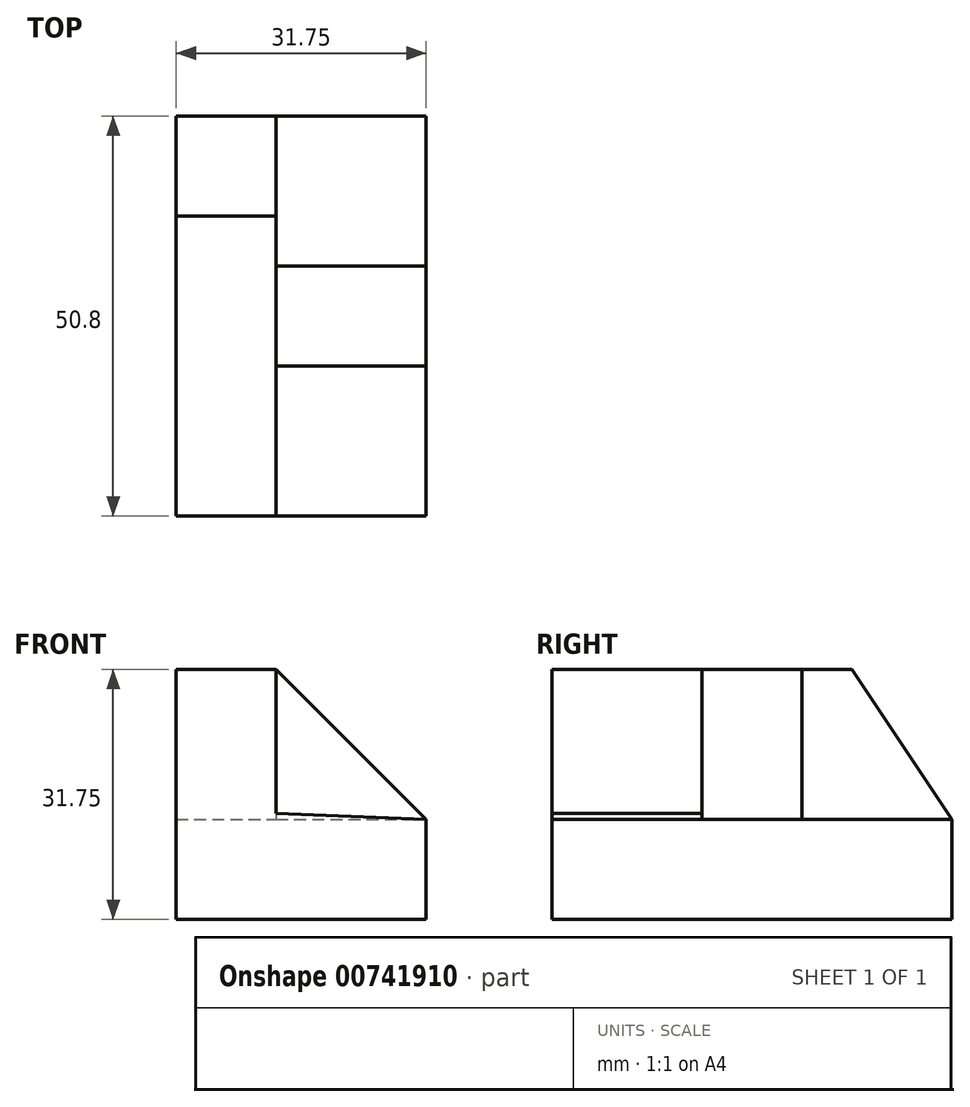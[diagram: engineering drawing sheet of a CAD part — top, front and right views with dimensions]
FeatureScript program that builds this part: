
annotation { "Feature Type Name" : "Feature", "Feature Type Description" : "" }
export const myFeature = defineFeature(function(context is Context, id is Id, definition is map)
    precondition{}
    {
        {
            var Q0;
            Q0=qCreatedBy(makeId("Right.planeOp"),FACE);
            var sketch = newSketch(context, id + "F0", { "sketchPlane" : qUnion([Q0])});
            skLineSegment(sketch, "E0", {"start": v(0, 31.75) * mm, "end": v(0, 0) * mm});
            skLineSegment(sketch, "E1", {"start": v(0, 0) * mm, "end": v(-50.8, 0) * mm});
            skLineSegment(sketch, "E2", {"start": v(-50.8, 0) * mm, "end": v(-50.8, 31.75) * mm});
            skLineSegment(sketch, "E3", {"start": v(-50.8, 31.75) * mm, "end": v(0, 31.75) * mm});
            skSolve(sketch);
        }
        {
            var Q0;
            Q0=makeQuery(id+"F0.imprint","IMPRINT",FACE,{"disambiguationData":[TD([[makeQuery(id+"F0.imprint","IMPRINT",EDGE,{"derivedFrom":sQuery(id+"F0.wireOp",EDGE,"E0")}),-1.0]])]});
            extrude(context, id + "F1", {"entities" : qUnion([Q0]), "depth" : 31.75 * mm, "offsetDistance" : 25.4 * mm});
        }
        {
            var Q0;
            Q0=makeQuery(id+"F1.opExtrude","CAP_FACE",FACE,{"disambiguationData":[OSD([sQuery(id+"F0.wireOp",EDGE,"E0"),sQuery(id+"F0.wireOp",EDGE,"E1"),sQuery(id+"F0.wireOp",EDGE,"E2"),sQuery(id+"F0.wireOp",EDGE,"E3")])],"isStart":false});
            var sketch = newSketch(context, id + "F2", { "sketchPlane" : qUnion([Q0])});
            skLineSegment(sketch, "E4", {"start": v(-50.8, 31.75) * mm, "end": v(-12.7, 31.75) * mm});
            skLineSegment(sketch, "E5", {"start": v(-12.7, 31.75) * mm, "end": v(0, 12.7) * mm});
            skLineSegment(sketch, "E6", {"start": v(0, 12.7) * mm, "end": v(0, 0) * mm});
            skLineSegment(sketch, "E7", {"start": v(0, 0) * mm, "end": v(0, 12.7) * mm});
            skSolve(sketch);
        }
        {
            var Q0;
            {var subQ0=sQuery(id+"F2.wireOp",EDGE,"E5");Q0=makeQuery(id+"F2.imprint","IMPRINT",FACE,{"disambiguationData":[TD([[makeQuery(id+"F2.imprint","IMPRINT",EDGE,{"derivedFrom":subQ0}),1.0]])]});}
            extrude(context, id + "F3", {"entities" : qUnion([Q0]), "operationType" : NewBodyOperationType.REMOVE, "endBound" : BoundingType.THROUGH_ALL, "oppositeDirection" : true, "depth" : 25.4 * mm, "offsetDistance" : 25.4 * mm});
        }
        {
            var Q0;
            Q0=makeQuery(id+"F1.opExtrude","CAP_FACE",FACE,{"disambiguationData":[OSD([sQuery(id+"F0.wireOp",EDGE,"E0"),sQuery(id+"F0.wireOp",EDGE,"E1"),sQuery(id+"F0.wireOp",EDGE,"E2"),sQuery(id+"F0.wireOp",EDGE,"E3")])],"isStart":false});
            var sketch = newSketch(context, id + "F4", { "sketchPlane" : qUnion([Q0])});
            skLineSegment(sketch, "E8", {"start": v(-12.7, 31.75) * mm, "end": v(-19.05, 31.75) * mm});
            skLineSegment(sketch, "E9", {"start": v(-19.05, 31.75) * mm, "end": v(-19.05, 12.7) * mm});
            skLineSegment(sketch, "E10", {"start": v(-19.05, 12.7) * mm, "end": v(0, 12.7) * mm});
            skSolve(sketch);
        }
        {
            var Q0;
            Q0=makeQuery(id+"F4.imprint","IMPRINT",FACE,{"disambiguationData":[TD([[makeQuery(id+"F4.imprint","IMPRINT",EDGE,{"derivedFrom":sQuery(id+"F4.wireOp",EDGE,"E8")}),-1.0]])]});
            extrude(context, id + "F5", {"entities" : qUnion([Q0]), "operationType" : NewBodyOperationType.REMOVE, "oppositeDirection" : true, "depth" : 19.05 * mm, "offsetDistance" : 25.4 * mm});
        }
        {
            var Q0;
            Q0=makeQuery(id+"F5.boolean.opBoolean","COPY",FACE,{"derivedFrom":makeQuery(id+"F5.opExtrude","SWEPT_FACE",FACE,{"disambiguationData":[OSD([sQuery(id+"F4.wireOp",EDGE,"E9")])]})});
            var sketch = newSketch(context, id + "F6", { "sketchPlane" : qUnion([Q0])});
            skLineSegment(sketch, "E11", {"start": v(-12.7, 31.75) * mm, "end": v(-31.75, 12.7) * mm});
            skSolve(sketch);
        }
        {
            var Q0;
            Q0=makeQuery(id+"F6.imprint","IMPRINT",FACE,{"disambiguationData":[TD([[makeQuery(id+"F6.imprint","IMPRINT",EDGE,{"derivedFrom":sQuery(id+"F6.wireOp",EDGE,"E11")}),-1.0]])]});
            extrude(context, id + "F7", {"entities" : qUnion([Q0]), "operationType" : NewBodyOperationType.REMOVE, "endBound" : BoundingType.THROUGH_ALL, "oppositeDirection" : true, "depth" : 25.4 * mm, "offsetDistance" : 25.4 * mm});
        }
        {
            var Q0;
            Q0=makeQuery(id+"F1.opExtrude","SWEPT_FACE",FACE,{"disambiguationData":[OSD([sQuery(id+"F0.wireOp",EDGE,"E2")])]});
            var sketch = newSketch(context, id + "F8", { "sketchPlane" : qUnion([Q0])});
            skLineSegment(sketch, "E12", {"start": v(12.7, 31.75) * mm, "end": v(12.7, 13.5) * mm});
            skLineSegment(sketch, "E13", {"start": v(12.7, 13.5) * mm, "end": v(31.75, 12.7) * mm});
            skSolve(sketch);
        }
        {
            var Q0;
            Q0=makeQuery(id+"F8.imprint","IMPRINT",FACE,{"disambiguationData":[TD([[makeQuery(id+"F8.imprint","IMPRINT",EDGE,{"derivedFrom":sQuery(id+"F8.wireOp",EDGE,"E12")}),1.0]])]});
            extrude(context, id + "F9", {"entities" : qUnion([Q0]), "operationType" : NewBodyOperationType.REMOVE, "oppositeDirection" : true, "depth" : 19.05 * mm, "offsetDistance" : 25.4 * mm});
        }
    });
